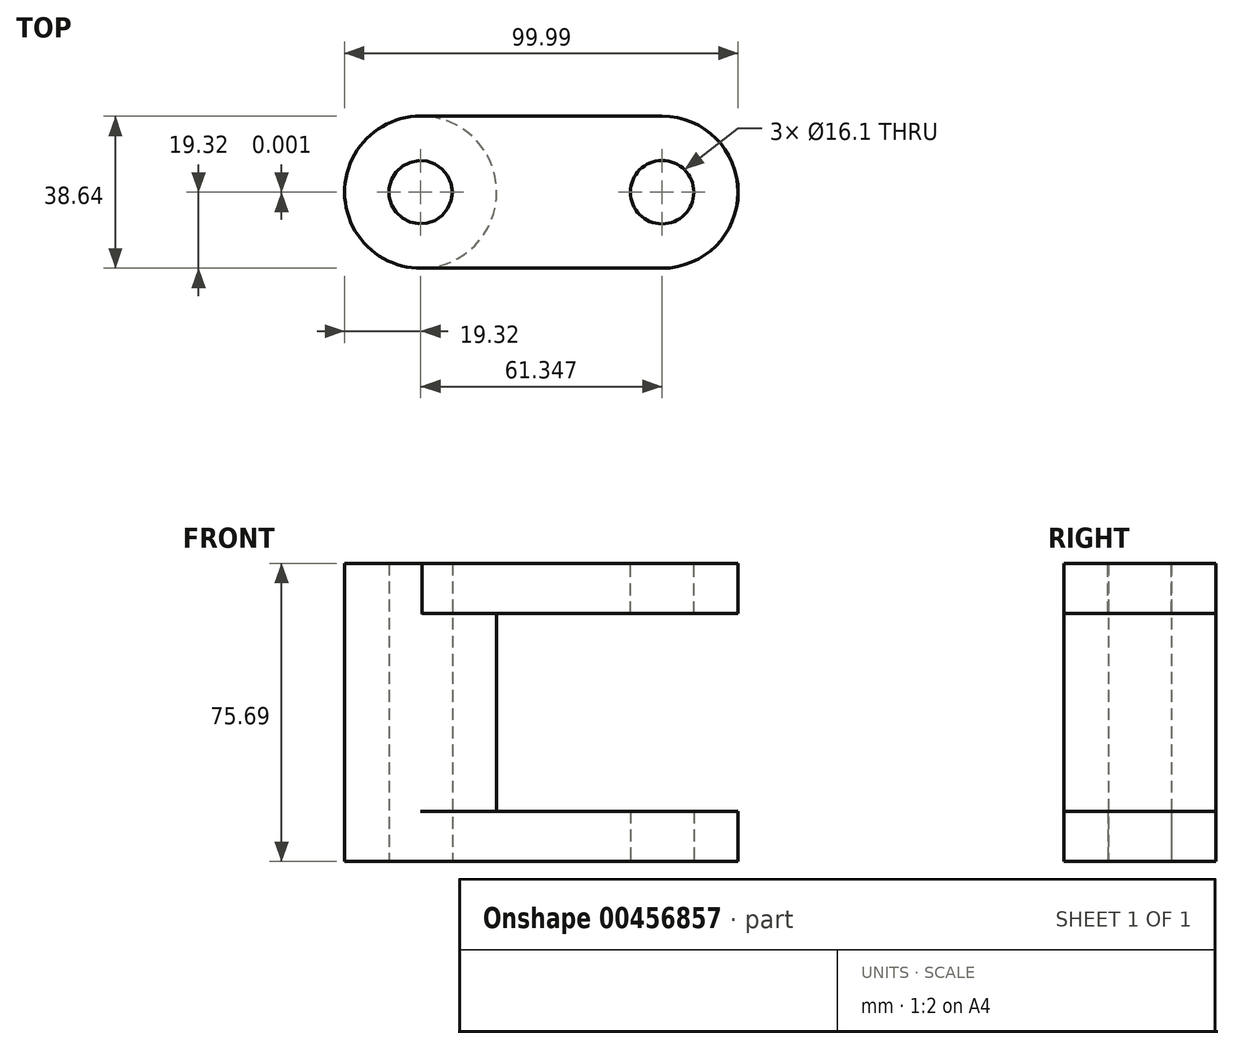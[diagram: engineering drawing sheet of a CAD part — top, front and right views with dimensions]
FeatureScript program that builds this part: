
annotation { "Feature Type Name" : "Feature", "Feature Type Description" : "" }
export const myFeature = defineFeature(function(context is Context, id is Id, definition is map)
    precondition{}
    {
        {
            var Q0;
            Q0=qCreatedBy(makeId("Top.planeOp"),FACE);
            var sketch = newSketch(context, id + "F0", { "sketchPlane" : qUnion([Q0])});
            skCircle(sketch, "E0", {"center": v(0, 0) * mm, "radius": 8.05 * mm});
            skCircle(sketch, "E1", {"center": v(0, 0) * mm, "radius": 19.32 * mm});
            skLineSegment(sketch, "E2.bottom", {"start": v(0, -19.32) * mm, "end": v(61.35, -19.32) * mm});
            skLineSegment(sketch, "E2.top", {"start": v(0, 19.32) * mm, "end": v(61.35, 19.32) * mm});
            skLineSegment(sketch, "E2.left", {"start": v(0, -19.32) * mm, "end": v(0, 19.32) * mm});
            skLineSegment(sketch, "E2.right", {"start": v(61.35, -19.32) * mm, "end": v(61.35, 19.32) * mm});
            skCircle(sketch, "E3", {"center": v(61.35, 0) * mm, "radius": 8.05 * mm});
            skCircle(sketch, "E4", {"center": v(61.35, 0) * mm, "radius": 19.32 * mm});
            skSolve(sketch);
        }
        {
            var Q0;
            Q0 = qSketchRegion(id + "F0", true);
            extrude(context, id + "F1", {"entities" : qUnion([Q0]), "depth" : 12.7 * mm, "offsetDistance" : 25.4 * mm});
        }
        {
            var Q0;
            {var subQ0=sQuery(id+"F0.wireOp",EDGE,"E2.left");var subQ1=sQuery(id+"F0.wireOp",EDGE,"E0");var subQ2=makeQuery(id+"F0.imprint","INTERSECT",VERTEX,{"disambiguationData":[OD(0.0)],"derivedFrom":[subQ1,subQ0]});Q0=makeQuery(id+"F0.imprint","IMPRINT",FACE,{"disambiguationData":[TD([[makeQuery(id+"F0.imprint","IMPRINT",EDGE,{"disambiguationData":[TD([[subQ2,-1.0]])],"derivedFrom":subQ1}),-1.0]])]});}
            var Q1;
            {var subQ0=sQuery(id+"F0.wireOp",EDGE,"E2.left");var subQ1=sQuery(id+"F0.wireOp",EDGE,"E0");var subQ2=makeQuery(id+"F0.imprint","INTERSECT",VERTEX,{"disambiguationData":[OD(0.0)],"derivedFrom":[subQ1,subQ0]});Q1=makeQuery(id+"F0.imprint","IMPRINT",FACE,{"disambiguationData":[TD([[makeQuery(id+"F0.imprint","IMPRINT",EDGE,{"disambiguationData":[TD([[subQ2,1.0]])],"derivedFrom":subQ1}),-1.0]])]});}
            extrude(context, id + "F2", {"entities" : qUnion([Q0, Q1]), "operationType" : NewBodyOperationType.ADD, "depth" : 75.7 * mm, "offsetDistance" : 25.4 * mm});
        }
        {
            var Q0;
            Q0=makeQuery(id+"F2.opExtrude","CAP_FACE",FACE,{"disambiguationData":[OSD([sQuery(id+"F0.wireOp",EDGE,"E0"),sQuery(id+"F0.wireOp",EDGE,"E1")])],"isStart":false});
            var sketch = newSketch(context, id + "F3", { "sketchPlane" : qUnion([Q0])});
            skLineSegment(sketch, "E5.bottom", {"start": v(0, 19.32) * mm, "end": v(61.34, 19.32) * mm});
            skLineSegment(sketch, "E5.top", {"start": v(0, -19.32) * mm, "end": v(61.34, -19.32) * mm});
            skLineSegment(sketch, "E5.left", {"start": v(0, 19.32) * mm, "end": v(0, -19.32) * mm});
            skLineSegment(sketch, "E5.right", {"start": v(61.34, 19.32) * mm, "end": v(61.34, -19.32) * mm});
            skCircle(sketch, "E6", {"center": v(0, 0) * mm, "radius": 8.05 * mm});
            skCircle(sketch, "E7", {"center": v(0, 0) * mm, "radius": 19.32 * mm});
            skCircle(sketch, "E8", {"center": v(61.34, 0) * mm, "radius": 8.05 * mm});
            skCircle(sketch, "E9", {"center": v(61.34, 0) * mm, "radius": 19.32 * mm});
            skSolve(sketch);
        }
        {
            var Q0;
            Q0 = qSketchRegion(id + "F3", true);
            extrude(context, id + "F4", {"entities" : qUnion([Q0]), "operationType" : NewBodyOperationType.ADD, "oppositeDirection" : true, "depth" : 12.7 * mm, "offsetDistance" : 25.4 * mm});
        }
    });
